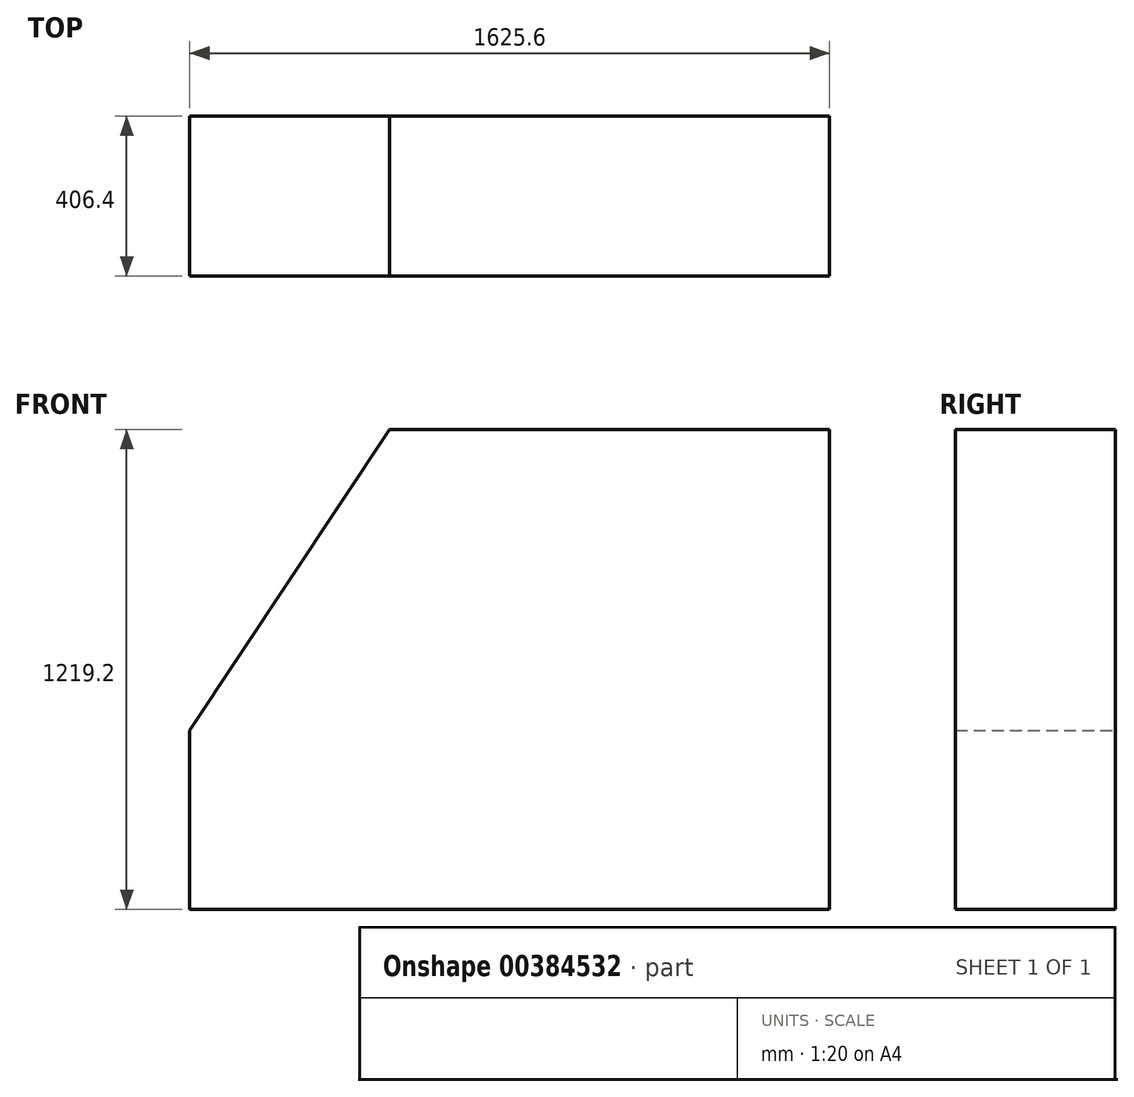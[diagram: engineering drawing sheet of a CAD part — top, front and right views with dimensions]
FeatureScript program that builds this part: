
annotation { "Feature Type Name" : "Feature", "Feature Type Description" : "" }
export const myFeature = defineFeature(function(context is Context, id is Id, definition is map)
    precondition{}
    {
        {
            var Q0;
            Q0=qCreatedBy(makeId("Front.planeOp"),FACE);
            var sketch = newSketch(context, id + "F0", { "sketchPlane" : qUnion([Q0])});
            skLineSegment(sketch, "E0", {"start": v(0, 0) * mm, "end": v(1625.6, 0) * mm});
            skLineSegment(sketch, "E1", {"start": v(1625.6, 0) * mm, "end": v(1625.6, 1219.2) * mm});
            skLineSegment(sketch, "E2", {"start": v(1625.6, 1219.2) * mm, "end": v(508, 1219.2) * mm});
            skLineSegment(sketch, "E3", {"start": v(0, 454.72) * mm, "end": v(0, 0) * mm});
            skLineSegment(sketch, "E4", {"start": v(0, 454.72) * mm, "end": v(508, 1219.2) * mm});
            skPoint(sketch, "E5.orphan", {"position": v(0, 1219.2) * mm});
            skSolve(sketch);
        }
        {
            var Q0;
            Q0 = qSketchRegion(id + "F0", true);
            extrude(context, id + "F1", {"entities" : qUnion([Q0]), "depth" : 406.4 * mm});
        }
    });
